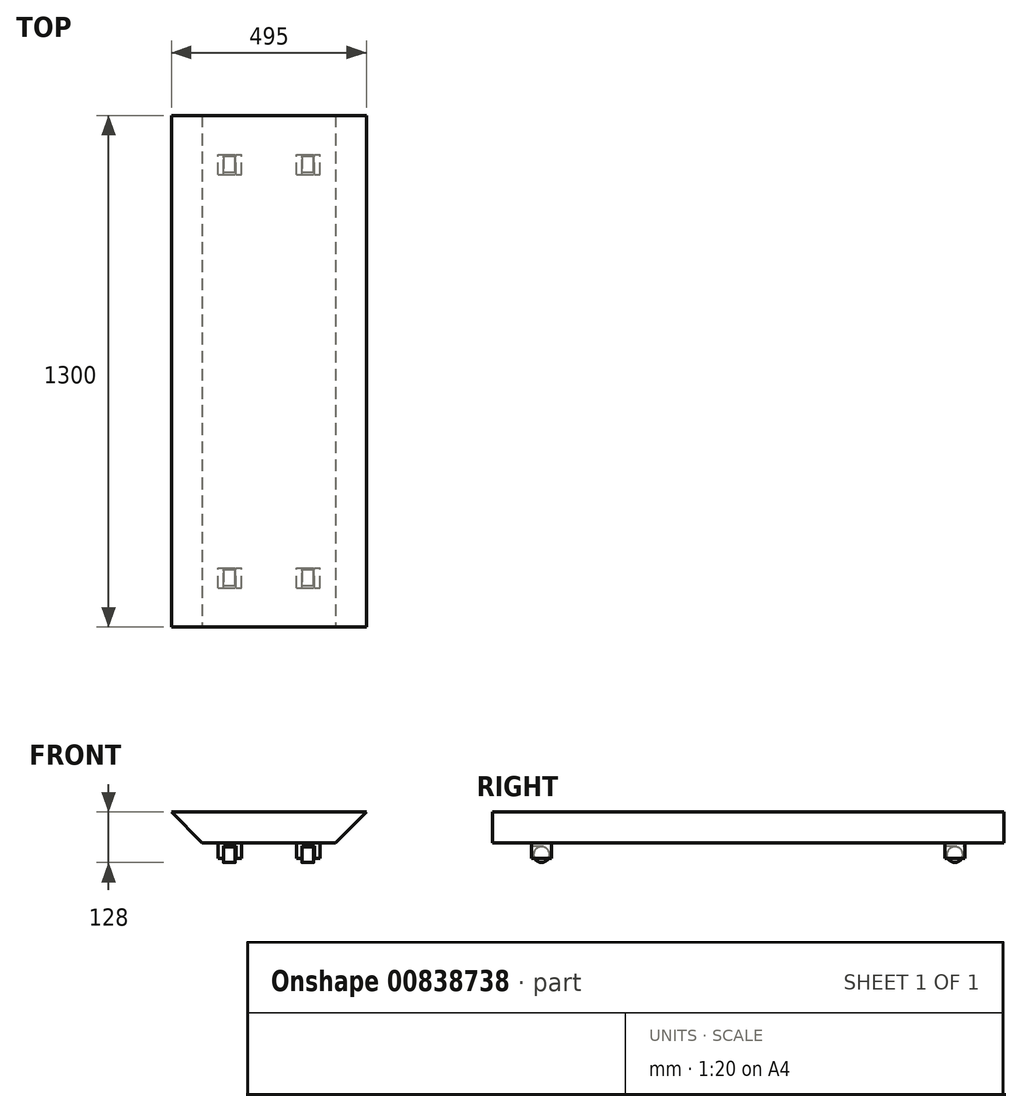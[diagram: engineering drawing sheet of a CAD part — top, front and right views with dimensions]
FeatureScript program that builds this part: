
annotation { "Feature Type Name" : "Feature", "Feature Type Description" : "" }
export const myFeature = defineFeature(function(context is Context, id is Id, definition is map)
    precondition{}
    {
        {
            var Q0;
            Q0=qCreatedBy(makeId("Front.planeOp"),FACE);
            var sketch = newSketch(context, id + "F0", { "sketchPlane" : qUnion([Q0])});
            skLineSegment(sketch, "E0", {"start": v(0, 80.5) * mm, "end": v(80.5, 0) * mm});
            skLineSegment(sketch, "E1", {"start": v(80.5, 0) * mm, "end": v(419.5, 0) * mm});
            skLineSegment(sketch, "E2", {"start": v(419.5, 0) * mm, "end": v(500, 80.5) * mm});
            skLineSegment(sketch, "E3", {"start": v(500, 80.5) * mm, "end": v(0, 80.5) * mm});
            skLineSegment(sketch, "E4", {"start": v(-66.53, 40.25) * mm, "end": v(659.57, 40.25) * mm, "construction": true});
            skSolve(sketch);
        }
        {
            var Q0;
            Q0 = qSketchRegion(id + "F0", true);
            extrude(context, id + "F1", {"entities" : qUnion([Q0]), "oppositeDirection" : true, "depth" : 1300 * mm, "offsetDistance" : 25 * mm});
        }
        {
            var Q0;
            Q0=makeQuery(id+"F1.opExtrude","CAP_FACE",FACE,{"disambiguationData":[OSD([sQuery(id+"F0.wireOp",EDGE,"E0"),sQuery(id+"F0.wireOp",EDGE,"E1"),sQuery(id+"F0.wireOp",EDGE,"E2"),sQuery(id+"F0.wireOp",EDGE,"E3")])],"isStart":true});
            var sketch = newSketch(context, id + "F2", { "sketchPlane" : qUnion([Q0])});
            skLineSegment(sketch, "E5.bottom", {"start": v(0, 129.09) * mm, "end": v(500, 129.09) * mm});
            skLineSegment(sketch, "E5.top", {"start": v(0, 78) * mm, "end": v(500, 78) * mm});
            skLineSegment(sketch, "E5.left", {"start": v(0, 129.09) * mm, "end": v(0, 78) * mm});
            skLineSegment(sketch, "E5.right", {"start": v(500, 129.09) * mm, "end": v(500, 78) * mm});
            skSolve(sketch);
        }
        {
            var Q0;
            Q0 = qSketchRegion(id + "F2", true);
            extrude(context, id + "F3", {"entities" : qUnion([Q0]), "operationType" : NewBodyOperationType.REMOVE, "oppositeDirection" : true, "depth" : 1300 * mm, "offsetDistance" : 25 * mm});
        }
        {
            var Q0;
            Q0=makeQuery(id+"F1.opExtrude","SWEPT_FACE",FACE,{"disambiguationData":[OSD([sQuery(id+"F0.wireOp",EDGE,"E1")])]});
            var sketch = newSketch(context, id + "F4", { "sketchPlane" : qUnion([Q0])});
            skLineSegment(sketch, "E6.bottom", {"start": v(120.5, -100) * mm, "end": v(180.5, -100) * mm});
            skLineSegment(sketch, "E6.top", {"start": v(120.5, -150) * mm, "end": v(180.5, -150) * mm});
            skLineSegment(sketch, "E6.left", {"start": v(120.5, -100) * mm, "end": v(120.5, -150) * mm});
            skLineSegment(sketch, "E6.right", {"start": v(180.5, -100) * mm, "end": v(180.5, -150) * mm});
            skLineSegment(sketch, "E7.bottom", {"start": v(319.5, -100) * mm, "end": v(379.5, -100) * mm});
            skLineSegment(sketch, "E7.top", {"start": v(319.5, -150) * mm, "end": v(379.5, -150) * mm});
            skLineSegment(sketch, "E7.left", {"start": v(319.5, -100) * mm, "end": v(319.5, -150) * mm});
            skLineSegment(sketch, "E7.right", {"start": v(379.5, -100) * mm, "end": v(379.5, -150) * mm});
            skLineSegment(sketch, "E8.bottom", {"start": v(120.5, -1150) * mm, "end": v(180.5, -1150) * mm});
            skLineSegment(sketch, "E8.top", {"start": v(120.5, -1200) * mm, "end": v(180.5, -1200) * mm});
            skLineSegment(sketch, "E8.left", {"start": v(120.5, -1150) * mm, "end": v(120.5, -1200) * mm});
            skLineSegment(sketch, "E8.right", {"start": v(180.5, -1150) * mm, "end": v(180.5, -1200) * mm});
            skLineSegment(sketch, "E9.bottom", {"start": v(319.5, -1150) * mm, "end": v(379.5, -1150) * mm});
            skLineSegment(sketch, "E9.top", {"start": v(319.5, -1200) * mm, "end": v(379.5, -1200) * mm});
            skLineSegment(sketch, "E9.left", {"start": v(319.5, -1150) * mm, "end": v(319.5, -1200) * mm});
            skLineSegment(sketch, "E9.right", {"start": v(379.5, -1150) * mm, "end": v(379.5, -1200) * mm});
            skSolve(sketch);
        }
        {
            var Q0;
            Q0 = qSketchRegion(id + "F4", true);
            extrude(context, id + "F5", {"entities" : qUnion([Q0]), "depth" : 40 * mm, "offsetDistance" : 25 * mm});
        }
        {
            var Q0;
            Q0=makeQuery(id+"F5.opExtrude","CAP_FACE",FACE,{"disambiguationData":[OSD([sQuery(id+"F4.wireOp",EDGE,"E6.bottom"),sQuery(id+"F4.wireOp",EDGE,"E6.top"),sQuery(id+"F4.wireOp",EDGE,"E6.left"),sQuery(id+"F4.wireOp",EDGE,"E6.right")])],"isStart":false});
            var sketch = newSketch(context, id + "F6", { "sketchPlane" : qUnion([Q0])});
            skLineSegment(sketch, "E10.bottom", {"start": v(134.5, -63.7) * mm, "end": v(166.5, -63.7) * mm});
            skLineSegment(sketch, "E10.top", {"start": v(134.5, -189.16) * mm, "end": v(166.5, -189.16) * mm});
            skLineSegment(sketch, "E10.left", {"start": v(134.5, -63.7) * mm, "end": v(134.5, -189.16) * mm});
            skLineSegment(sketch, "E10.right", {"start": v(166.5, -63.7) * mm, "end": v(166.5, -189.16) * mm});
            skPoint(sketch, "E11.oppositeSnap0", {"position": v(150.5, -189.16) * mm});
            skLineSegment(sketch, "E11.bottom", {"start": v(333.5, -63.7) * mm, "end": v(365.5, -63.7) * mm});
            skLineSegment(sketch, "E11.top", {"start": v(333.5, -189.16) * mm, "end": v(365.5, -189.16) * mm});
            skLineSegment(sketch, "E11.left", {"start": v(333.5, -63.7) * mm, "end": v(333.5, -189.16) * mm});
            skLineSegment(sketch, "E11.right", {"start": v(365.5, -63.7) * mm, "end": v(365.5, -189.16) * mm});
            skLineSegment(sketch, "E12.bottom", {"start": v(134.5, -1111.28) * mm, "end": v(166.5, -1111.28) * mm});
            skLineSegment(sketch, "E12.top", {"start": v(134.5, -1236.74) * mm, "end": v(166.5, -1236.74) * mm});
            skLineSegment(sketch, "E12.left", {"start": v(134.5, -1111.28) * mm, "end": v(134.5, -1236.74) * mm});
            skLineSegment(sketch, "E12.right", {"start": v(166.5, -1111.28) * mm, "end": v(166.5, -1236.74) * mm});
            skLineSegment(sketch, "E13.bottom", {"start": v(333.5, -1111.28) * mm, "end": v(365.5, -1111.28) * mm});
            skLineSegment(sketch, "E13.top", {"start": v(333.5, -1236.74) * mm, "end": v(365.5, -1236.74) * mm});
            skLineSegment(sketch, "E13.left", {"start": v(333.5, -1111.28) * mm, "end": v(333.5, -1236.74) * mm});
            skLineSegment(sketch, "E13.right", {"start": v(365.5, -1111.28) * mm, "end": v(365.5, -1236.74) * mm});
            skSolve(sketch);
        }
        {
            var Q0;
            Q0 = qSketchRegion(id + "F6", true);
            extrude(context, id + "F7", {"entities" : qUnion([Q0]), "operationType" : NewBodyOperationType.REMOVE, "oppositeDirection" : true, "depth" : 32 * mm, "offsetDistance" : 25 * mm});
        }
        {
            var Q0;
            Q0=makeQuery(id+"F7.boolean.opBoolean","COPY",FACE,{"derivedFrom":makeQuery(id+"F7.opExtrude","SWEPT_FACE",FACE,{"disambiguationData":[OSD([sQuery(id+"F6.wireOp",EDGE,"E10.left")])]})});
            var sketch = newSketch(context, id + "F8", { "sketchPlane" : qUnion([Q0])});
            skCircle(sketch, "E14", {"center": v(125, -30) * mm, "radius": 20 * mm});
            skCircle(sketch, "E15", {"center": v(1175, -30) * mm, "radius": 20 * mm});
            skSolve(sketch);
        }
        {
            var Q0;
            Q0 = qSketchRegion(id + "F8", true);
            extrude(context, id + "F9", {"entities" : qUnion([Q0]), "operationType" : NewBodyOperationType.ADD, "depth" : 30 * mm, "offsetDistance" : 25 * mm});
        }
        {
            var Q0;
            Q0=makeQuery(id+"F7.boolean.opBoolean","COPY",FACE,{"derivedFrom":makeQuery(id+"F7.opExtrude","SWEPT_FACE",FACE,{"disambiguationData":[OSD([sQuery(id+"F6.wireOp",EDGE,"E11.left")])]})});
            var sketch = newSketch(context, id + "F10", { "sketchPlane" : qUnion([Q0])});
            skCircle(sketch, "E16", {"center": v(125, -30) * mm, "radius": 20 * mm});
            skCircle(sketch, "E17", {"center": v(1175, -30) * mm, "radius": 20 * mm});
            skSolve(sketch);
        }
        {
            var Q0;
            Q0 = qSketchRegion(id + "F10", true);
            extrude(context, id + "F11", {"entities" : qUnion([Q0]), "operationType" : NewBodyOperationType.ADD, "depth" : 30 * mm, "offsetDistance" : 25 * mm});
        }
    });
